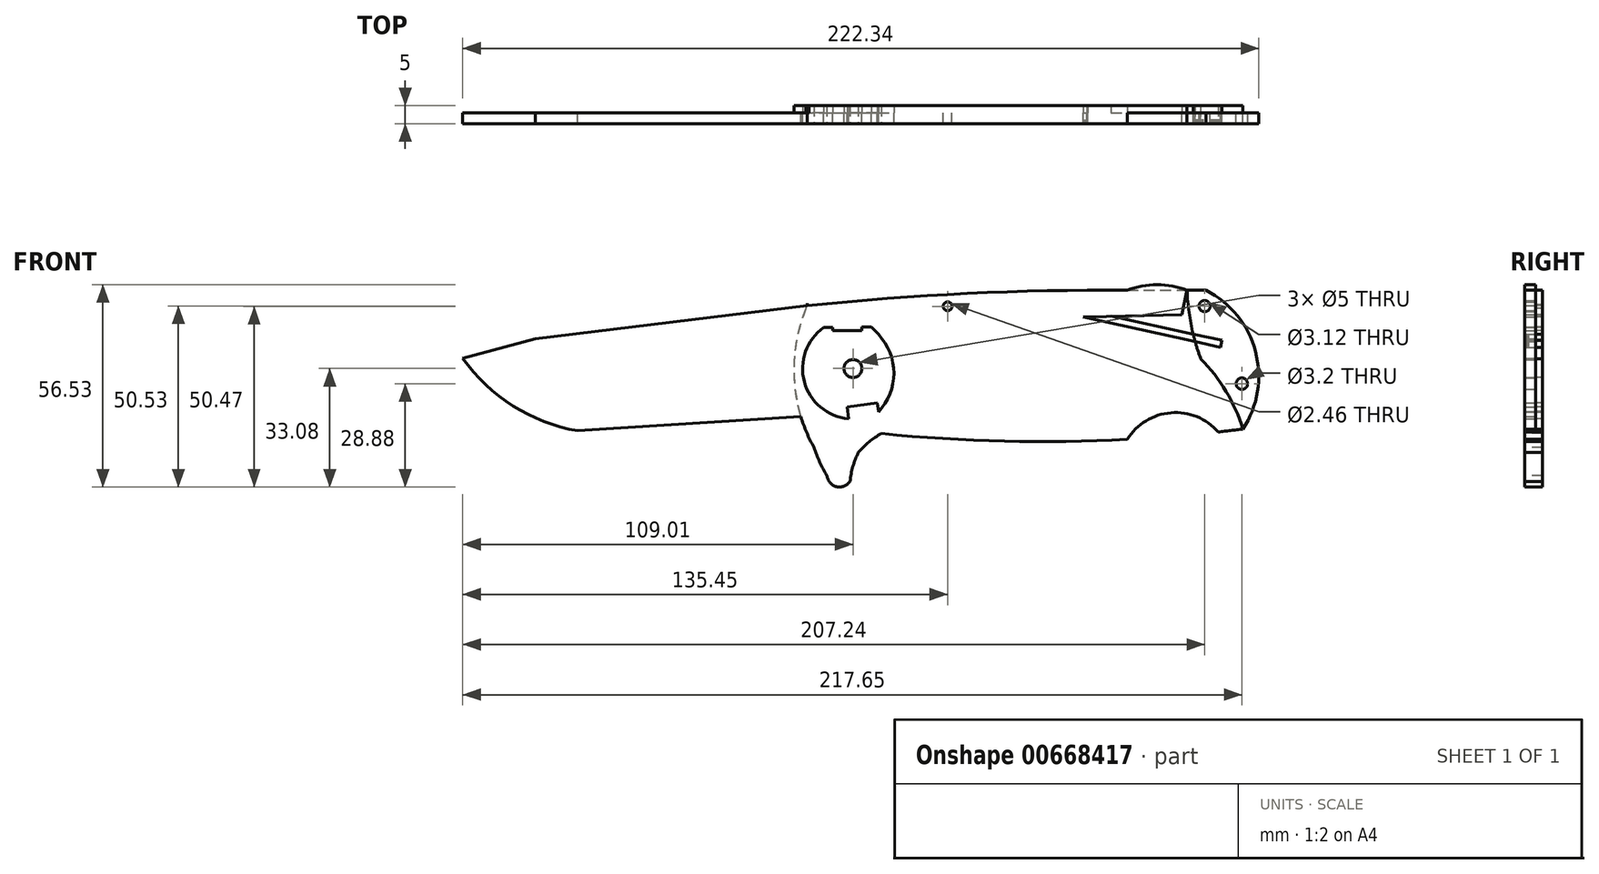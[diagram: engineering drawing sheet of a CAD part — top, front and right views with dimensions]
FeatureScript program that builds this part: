
annotation { "Feature Type Name" : "Feature", "Feature Type Description" : "" }
export const myFeature = defineFeature(function(context is Context, id is Id, definition is map)
    precondition{}
    {
        {
            var Q0;
            Q0=qCreatedBy(makeId("Front.planeOp"),FACE);
            var sketch = newSketch(context, id + "F0", { "sketchPlane" : qUnion([Q0])});
            skArc(sketch, "E0", {"start": v(38.96, -8.35) * mm, "mid": v(42.45, 13.33) * mm, "end": v(28.67, 30.42) * mm});
            skArc(sketch, "E1", {"start": v(-62.01, -9.6) * mm, "mid": v(-27.7, -11.74) * mm, "end": v(6.69, -11.23) * mm});
            skArc(sketch, "E2", {"start": v(-62.01, -9.6) * mm, "mid": v(-65.5, -11.93) * mm, "end": v(-68.47, -14.9) * mm});
            skArc(sketch, "E3", {"start": v(-80.85, -13.53) * mm, "mid": v(-79.28, -17.56) * mm, "end": v(-77.25, -21.38) * mm});
            skPoint(sketch, "E4.end.orphan", {"position": v(-73.1, -26.92) * mm});
            skArc(sketch, "E5", {"start": v(-77.25, -21.38) * mm, "mid": v(-74.57, -24.43) * mm, "end": v(-70.79, -22.98) * mm});
            skArc(sketch, "E6", {"start": v(-68.47, -14.9) * mm, "mid": v(-70, -18.84) * mm, "end": v(-70.79, -22.98) * mm});
            skCircle(sketch, "E7", {"center": v(-69.98, 8.55) * mm, "radius": 2.5 * mm});
            skArc(sketch, "E8", {"start": v(32.05, -9.17) * mm, "mid": v(18.85, -3.8) * mm, "end": v(6.69, -11.23) * mm});
            skArc(sketch, "E9.trimOffspring", {"start": v(32.05, -9.17) * mm, "mid": v(35.5, -8.77) * mm, "end": v(38.96, -8.35) * mm});
            skArc(sketch, "E10", {"start": v(6.66, 30.42) * mm, "mid": v(15, 26.76) * mm, "end": v(23.35, 30.42) * mm});
            skLineSegment(sketch, "E11.trimOffspring", {"start": v(23.35, 30.42) * mm, "end": v(28.67, 30.42) * mm});
            skArc(sketch, "E12", {"start": v(-82.74, 26.12) * mm, "mid": v(-86.44, 6.07) * mm, "end": v(-80.85, -13.53) * mm});
            skArc(sketch, "E13", {"start": v(6.66, 30.42) * mm, "mid": v(-38.1, 29.51) * mm, "end": v(-82.74, 26.12) * mm});
            skArc(sketch, "E14", {"start": v(23.35, 30.42) * mm, "mid": v(24.5, 20.7) * mm, "end": v(27.17, 11.28) * mm});
            skLineSegment(sketch, "E15", {"start": v(21.88, 23.6) * mm, "end": v(23.35, 30.42) * mm});
            skLineSegment(sketch, "E16", {"start": v(-74.78, 26.9) * mm, "end": v(-75.59, 21.45) * mm});
            skLineSegment(sketch, "E17", {"start": v(6.66, 30.42) * mm, "end": v(23.35, 30.42) * mm});
            skLineSegment(sketch, "E18.left", {"start": v(-75.59, 21.45) * mm, "end": v(-75.59, 19.1) * mm});
            skLineSegment(sketch, "E18.right", {"start": v(-67.57, 21.63) * mm, "end": v(-67.57, 19.2) * mm});
            skLineSegment(sketch, "E19", {"start": v(-67.57, 21.63) * mm, "end": v(21.88, 23.6) * mm});
            skCircle(sketch, "E20", {"center": v(-43.54, 25.94) * mm, "radius": 1.23 * mm});
            skLineSegment(sketch, "E21", {"start": v(25.06, 18.18) * mm, "end": v(2.12, 23.17) * mm});
            skLineSegment(sketch, "E22", {"start": v(2.12, 23.17) * mm, "end": v(33.07, 16.44) * mm});
            skLineSegment(sketch, "E23", {"start": v(33.07, 16.44) * mm, "end": v(32.65, 14.49) * mm});
            skLineSegment(sketch, "E24", {"start": v(32.65, 14.49) * mm, "end": v(-5.64, 23) * mm});
            skLineSegment(sketch, "E25", {"start": v(-5.64, 23) * mm, "end": v(-4.61, 23.02) * mm});
            skLineSegment(sketch, "E26", {"start": v(-4.61, 23.02) * mm, "end": v(2.8, 23.02) * mm});
            skArc(sketch, "E27", {"start": v(23.35, 30.42) * mm, "mid": v(15, 32) * mm, "end": v(6.66, 30.42) * mm});
            skLineSegment(sketch, "E28", {"start": v(-75.59, 21.45) * mm, "end": v(-75.59, 21.45) * mm});
            skPoint(sketch, "E29.end.orphan", {"position": v(-75.59, 20.8) * mm});
            skArc(sketch, "E30", {"start": v(-78.16, 19.99) * mm, "mid": v(-83.55, 4.86) * mm, "end": v(-71.25, -5.46) * mm});
            skLineSegment(sketch, "E31", {"start": v(-78.16, 19.99) * mm, "end": v(-75.59, 20.03) * mm});
            skPoint(sketch, "E32.end.orphan", {"position": v(-62.2, 20.27) * mm});
            skPoint(sketch, "E33.endSnap0", {"position": v(-66.22, 20.2) * mm});
            skPoint(sketch, "E34.orphan", {"position": v(-64.88, 20.22) * mm});
            skPoint(sketch, "E35.trimOffspring.start.orphan", {"position": v(-67.57, 20.17) * mm});
            skLineSegment(sketch, "E36", {"start": v(-67.57, 20.17) * mm, "end": v(-64.85, 20.19) * mm});
            skLineSegment(sketch, "E37", {"start": v(-67.57, 18.1) * mm, "end": v(-67.57, 17.95) * mm});
            skLineSegment(sketch, "E38", {"start": v(-75.59, 18.1) * mm, "end": v(-75.59, 17.95) * mm});
            skLineSegment(sketch, "E39", {"start": v(-75.59, 19.1) * mm, "end": v(-67.57, 19.2) * mm});
            skLineSegment(sketch, "E40", {"start": v(-64.88, 20.22) * mm, "end": v(-62.87, 18.1) * mm});
            skPoint(sketch, "E41.orphan", {"position": v(-62.87, 20.2) * mm});
            skLineSegment(sketch, "E42", {"start": v(-78.16, 19.99) * mm, "end": v(-82.74, 26.12) * mm});
            skLineSegment(sketch, "E43", {"start": v(-82.74, 26.12) * mm, "end": v(-82.74, 26.12) * mm});
            skPoint(sketch, "E44.start.orphan", {"position": v(-191.79, 19.58) * mm});
            skLineSegment(sketch, "E45", {"start": v(-84.04, -6.39) * mm, "end": v(-84, -6.38) * mm});
            skLineSegment(sketch, "E46", {"start": v(-75.59, 19.1) * mm, "end": v(-75.59, 17.95) * mm, "construction": true});
            skPoint(sketch, "E47.start.orphan", {"position": v(-84.04, -6.38) * mm});
            skArc(sketch, "E48", {"start": v(38.96, -8.35) * mm, "mid": v(34.25, 2.18) * mm, "end": v(27.17, 11.28) * mm});
            skPoint(sketch, "E49.orphan", {"position": v(-137.26, 22.85) * mm});
            skLineSegment(sketch, "E50", {"start": v(-74.9, 26.12) * mm, "end": v(-84.7, 25.19) * mm});
            skArc(sketch, "E51", {"start": v(-62.87, -3.59) * mm, "mid": v(-58.55, 7.25) * mm, "end": v(-62.87, 18.1) * mm});
            skLineSegment(sketch, "E52", {"start": v(-75.59, -4.35) * mm, "end": v(-146.9, -8.83) * mm});
            skArc(sketch, "E53", {"start": v(-178.99, 11.44) * mm, "mid": v(-164.95, -1.88) * mm, "end": v(-146.9, -8.83) * mm});
            skPoint(sketch, "E54.start.orphan", {"position": v(-176.27, 12.79) * mm});
            skCircle(sketch, "E55", {"center": v(38.66, 4.35) * mm, "radius": 1.6 * mm});
            skCircle(sketch, "E56", {"center": v(28.25, 26) * mm, "radius": 1.56 * mm});
            skPoint(sketch, "E57.endSnap0", {"position": v(-71.58, 19.15) * mm});
            skPoint(sketch, "E58.orphan", {"position": v(-70.1, 19.15) * mm});
            skLineSegment(sketch, "E59", {"start": v(-178.99, 11.44) * mm, "end": v(-158.64, 16.83) * mm});
            skPoint(sketch, "E60.orphan", {"position": v(-179.91, 12.79) * mm});
            skLineSegment(sketch, "E61", {"start": v(-82.74, 26.12) * mm, "end": v(-158.64, 16.83) * mm});
            skPoint(sketch, "E62.start.orphan", {"position": v(-75.59, -3.76) * mm});
            skLineSegment(sketch, "E63", {"start": v(-62.87, -3.48) * mm, "end": v(-62.87, -3.59) * mm});
            skLineSegment(sketch, "E64", {"start": v(-71.25, -5.46) * mm, "end": v(-71.6, -2.16) * mm});
            skLineSegment(sketch, "E65", {"start": v(-63.2, -1.04) * mm, "end": v(-71.6, -2.16) * mm});
            skLineSegment(sketch, "E66", {"start": v(-62.87, -3.48) * mm, "end": v(-63.2, -1.04) * mm});
            skSolve(sketch);
        }
        {
            var Q0;
            Q0=makeQuery(id+"F0.imprint","IMPRINT",FACE,{"disambiguationData":[TD([[makeQuery(id+"F0.imprint","IMPRINT",EDGE,{"derivedFrom":sQuery(id+"F0.wireOp",EDGE,"E0")}),1.0]])]});
            extrude(context, id + "F1", {"entities" : qUnion([Q0]), "depth" : 2.5 * mm, "offsetDistance" : 25 * mm});
        }
        {
            var Q0;
            Q0=makeQuery(id+"F1.opExtrude","SWEPT_EDGE",EDGE,{"disambiguationData":[OSD([sQuery(id+"F0.wireOp",EDGE,"E0"),sQuery(id+"F0.wireOp",EDGE,"E11.trimOffspring")])]});
            fillet(context, id + "F2", {"entities" : qUnion([Q0]), "radius" : 5 * mm, "tangentPropagation" : true, "allowEdgeOverflow" : false});
        }
        {
            var Q0;
            Q0=makeQuery(id+"F1.opExtrude","SWEPT_EDGE",EDGE,{"disambiguationData":[OSD([sQuery(id+"F0.wireOp",EDGE,"E0"),sQuery(id+"F0.wireOp",EDGE,"E9.trimOffspring")])]});
            fillet(context, id + "F3", {"entities" : qUnion([Q0]), "radius" : 5 * mm, "tangentPropagation" : true, "allowEdgeOverflow" : false});
        }
        {
            var Q0;
            Q0=makeQuery(id+"F0.imprint","IMPRINT",FACE,{"disambiguationData":[TD([[makeQuery(id+"F0.imprint","IMPRINT",EDGE,{"derivedFrom":sQuery(id+"F0.wireOp",EDGE,"E0")}),1.0]])]});
            extrude(context, id + "F4", {"entities" : qUnion([Q0]), "operationType" : NewBodyOperationType.ADD, "oppositeDirection" : true, "depth" : 3 * mm, "offsetDistance" : 25 * mm});
        }
        {
            var Q0;
            Q0=makeQuery(id+"F0.imprint","IMPRINT",FACE,{"disambiguationData":[TD([[makeQuery(id+"F0.imprint","IMPRINT",EDGE,{"derivedFrom":sQuery(id+"F0.wireOp",EDGE,"E10")}),1.0]])]});
            extrude(context, id + "F5", {"entities" : qUnion([Q0]), "depth" : 3 * mm, "offsetDistance" : 25 * mm});
        }
        {
            var Q0;
            {var subQ2=sQuery(id+"F0.wireOp",EDGE,"E10");Q0=makeQuery(id+"F0.imprint","IMPRINT",FACE,{"disambiguationData":[TD([[makeQuery(id+"F0.imprint","IMPRINT",EDGE,{"derivedFrom":subQ2}),-1.0]])]});}
            extrude(context, id + "F6", {"entities" : qUnion([Q0]), "depth" : 3 * mm, "offsetDistance" : 25 * mm});
        }
        {
            var Q0;
            {var subQ0=sQuery(id+"F0.wireOp",EDGE,"E25");Q0=makeQuery(id+"F0.imprint","IMPRINT",FACE,{"disambiguationData":[TD([[makeQuery(id+"F0.imprint","IMPRINT",EDGE,{"derivedFrom":subQ0}),-1.0]])]});}
            var Q1;
            {var subQ5=sQuery(id+"F0.wireOp",EDGE,"E23");Q1=makeQuery(id+"F0.imprint","IMPRINT",FACE,{"disambiguationData":[TD([[makeQuery(id+"F0.imprint","IMPRINT",EDGE,{"derivedFrom":subQ5}),-1.0]])]});}
            extrude(context, id + "F7", {"entities" : qUnion([Q0, Q1]), "depth" : 2 * mm, "offsetDistance" : 25 * mm});
        }
        {
            var Q0;
            Q0=makeQuery(id+"F0.imprint","IMPRINT",FACE,{"disambiguationData":[TD([[makeQuery(id+"F0.imprint","IMPRINT",EDGE,{"derivedFrom":sQuery(id+"F0.wireOp",EDGE,"E17")}),1.0]])]});
            extrude(context, id + "F8", {"entities" : qUnion([Q0]), "operationType" : NewBodyOperationType.ADD, "depth" : 3 * mm, "offsetDistance" : 25 * mm});
        }
        {
            var Q0;
            Q0=makeQuery(id+"F4.opExtrude","CAP_FACE",FACE,{"disambiguationData":[OSD([sQuery(id+"F0.wireOp",EDGE,"E0"),sQuery(id+"F0.wireOp",EDGE,"E11.trimOffspring"),sQuery(id+"F0.wireOp",EDGE,"E14"),sQuery(id+"F0.wireOp",EDGE,"E22"),sQuery(id+"F0.wireOp",EDGE,"E23"),sQuery(id+"F0.wireOp",EDGE,"E24")])],"isStart":false});
            extrude(context, id + "F9", {"entities" : qUnion([Q0]), "operationType" : NewBodyOperationType.ADD, "depth" : 1 * mm, "offsetDistance" : 25 * mm});
        }
        {
            var Q0;
            Q0=makeQuery(id+"F9.opExtrude","CAP_FACE",FACE,{"disambiguationData":[OSD([sQuery(id+"F0.wireOp",EDGE,"E0"),sQuery(id+"F0.wireOp",EDGE,"E11.trimOffspring"),sQuery(id+"F0.wireOp",EDGE,"E14"),sQuery(id+"F0.wireOp",EDGE,"E22"),sQuery(id+"F0.wireOp",EDGE,"E23"),sQuery(id+"F0.wireOp",EDGE,"E24")])],"isStart":false});
            extrude(context, id + "F10", {"entities" : qUnion([Q0]), "operationType" : NewBodyOperationType.REMOVE, "oppositeDirection" : true, "depth" : 2 * mm, "offsetDistance" : 25 * mm});
        }
        {
            var Q0;
            {var subQ11=sQuery(id+"F0.wireOp",EDGE,"E10");Q0=makeQuery(id+"F0.imprint","IMPRINT",FACE,{"disambiguationData":[TD([[makeQuery(id+"F0.imprint","IMPRINT",EDGE,{"derivedFrom":subQ11}),-1.0]])]});}
            var Q1;
            Q1=makeQuery(id+"F0.imprint","IMPRINT",FACE,{"disambiguationData":[TD([[makeQuery(id+"F0.imprint","IMPRINT",EDGE,{"derivedFrom":sQuery(id+"F0.wireOp",EDGE,"E10")}),1.0]])]});
            extrude(context, id + "F11", {"entities" : qUnion([Q0, Q1]), "oppositeDirection" : true, "depth" : 2.5 * mm, "offsetDistance" : 25 * mm});
        }
        {
            var Q0;
            Q0=makeQuery(id+"F0.imprint","IMPRINT",FACE,{"disambiguationData":[TD([[makeQuery(id+"F0.imprint","IMPRINT",EDGE,{"derivedFrom":sQuery(id+"F0.wireOp",EDGE,"d4K3JjEk-ksbC-rxim-k1ym-PkVV789aZZM4")}),-1.0]])]});
            var Q1;
            Q1=makeQuery(id+"F0.imprint","IMPRINT",FACE,{"disambiguationData":[TD([[makeQuery(id+"F0.imprint","IMPRINT",EDGE,{"derivedFrom":sQuery(id+"F0.wireOp",EDGE,"E7")}),-1.0]])]});
            var Q2;
            {var subQ1=sQuery(id+"F0.wireOp",EDGE,"E42");Q2=makeQuery(id+"F0.imprint","IMPRINT",FACE,{"disambiguationData":[TD([[makeQuery(id+"F0.imprint","IMPRINT",EDGE,{"derivedFrom":subQ1}),1.0]])]});}
            var Q3;
            {var subQ2=sQuery(id+"F0.wireOp",EDGE,"E16");Q3=makeQuery(id+"F0.imprint","IMPRINT",FACE,{"disambiguationData":[TD([[makeQuery(id+"F0.imprint","IMPRINT",EDGE,{"derivedFrom":subQ2}),-1.0]])]});}
            extrude(context, id + "F12", {"entities" : qUnion([Q0, Q1, Q2, Q3]), "depth" : 3 * mm, "offsetDistance" : 25 * mm});
        }
        {
            var Q0;
            {var subQ1=sQuery(id+"F0.wireOp",EDGE,"E31");Q0=makeQuery(id+"F0.imprint","IMPRINT",FACE,{"disambiguationData":[TD([[makeQuery(id+"F0.imprint","IMPRINT",EDGE,{"derivedFrom":subQ1}),1.0]])]});}
            var Q1;
            {var subQ3=sQuery(id+"F0.wireOp",EDGE,"E12");var subQ7=sQuery(id+"F0.wireOp",EDGE,"E50");var subQ9=makeQuery(id+"F0.imprint","INTERSECT",VERTEX,{"derivedFrom":[subQ3,subQ7]});Q1=makeQuery(id+"F0.imprint","IMPRINT",FACE,{"disambiguationData":[TD([[makeQuery(id+"F0.imprint","IMPRINT",EDGE,{"disambiguationData":[TD([[subQ9,-1.0]])],"derivedFrom":subQ3}),1.0]])]});}
            extrude(context, id + "F13", {"entities" : qUnion([Q0, Q1]), "oppositeDirection" : true, "depth" : 2.5 * mm, "offsetDistance" : 25 * mm});
        }
        {
            var Q0;
            Q0=makeQuery(id+"F11.opExtrude","SWEPT_BODY",BODY,{"disambiguationData":[OSD([sQuery(id+"F0.wireOp",EDGE,"E13"),sQuery(id+"F0.wireOp",EDGE,"E15"),sQuery(id+"F0.wireOp",EDGE,"E16"),sQuery(id+"F0.wireOp",EDGE,"E17"),sQuery(id+"F0.wireOp",EDGE,"E18.left"),sQuery(id+"F0.wireOp",EDGE,"E18.right"),sQuery(id+"F0.wireOp",EDGE,"E19"),sQuery(id+"F0.wireOp",EDGE,"E20"),sQuery(id+"F0.wireOp",EDGE,"E25"),sQuery(id+"F0.wireOp",EDGE,"E39")])]});
            var Q1;
            Q1=makeQuery(id+"F13.opExtrude","SWEPT_BODY",BODY,{"disambiguationData":[OSD([sQuery(id+"F0.wireOp",EDGE,"E12"),sQuery(id+"F0.wireOp",EDGE,"E16"),sQuery(id+"F0.wireOp",EDGE,"E18.left"),sQuery(id+"F0.wireOp",EDGE,"E30"),sQuery(id+"F0.wireOp",EDGE,"E31"),sQuery(id+"F0.wireOp",EDGE,"gyOXoMPe-yHgR-Amyv-KbJH-xM9F0bznGJoQ"),sQuery(id+"F0.wireOp",EDGE,"E50")])]});
            booleanBodies(context, id + "F14", {"operationType" : BooleanOperationType.UNION, "tools" : qUnion([Q0, Q1])});
        }
        {
            var Q0;
            Q0=makeQuery(id+"F0.imprint","IMPRINT",FACE,{"disambiguationData":[TD([[makeQuery(id+"F0.imprint","IMPRINT",EDGE,{"derivedFrom":sQuery(id+"F0.wireOp",EDGE,"E7")}),-1.0]])]});
            var Q1;
            {var subQ4=sQuery(id+"F0.wireOp",EDGE,"d76b19db-baf5-4d0a-8a79-8b2ea7cbffe1");Q1=makeQuery(id+"F0.imprint","IMPRINT",FACE,{"disambiguationData":[TD([[makeQuery(id+"F0.imprint","IMPRINT",EDGE,{"derivedFrom":subQ4}),-1.0]])]});}
            var Q2;
            {var subQ3=sQuery(id+"F0.wireOp",EDGE,"E12");var subQ7=sQuery(id+"F0.wireOp",EDGE,"E50");var subQ9=makeQuery(id+"F0.imprint","INTERSECT",VERTEX,{"derivedFrom":[subQ3,subQ7]});Q2=makeQuery(id+"F0.imprint","IMPRINT",FACE,{"disambiguationData":[TD([[makeQuery(id+"F0.imprint","IMPRINT",EDGE,{"disambiguationData":[TD([[subQ9,-1.0]])],"derivedFrom":subQ3}),1.0]])]});}
            extrude(context, id + "F15", {"entities" : qUnion([Q0, Q1, Q2]), "depth" : 3 * mm, "offsetDistance" : 25 * mm});
        }
        {
            var Q0;
            {var subQ1=sQuery(id+"F0.wireOp",EDGE,"E31");Q0=makeQuery(id+"F0.imprint","IMPRINT",FACE,{"disambiguationData":[TD([[makeQuery(id+"F0.imprint","IMPRINT",EDGE,{"derivedFrom":subQ1}),1.0]])]});}
            extrude(context, id + "F16", {"entities" : qUnion([Q0]), "depth" : 3 * mm, "offsetDistance" : 25 * mm});
        }
        {
            var Q0;
            Q0=makeQuery(id+"F0.imprint","IMPRINT",FACE,{"disambiguationData":[TD([[makeQuery(id+"F0.imprint","IMPRINT",EDGE,{"derivedFrom":sQuery(id+"F0.wireOp",EDGE,"E0")}),1.0]])]});
            extrude(context, id + "F17", {"entities" : qUnion([Q0]), "depth" : 25 * mm, "offsetDistance" : 25 * mm});
        }
        {
            var Q0;
            {var subQ4=sQuery(id+"F0.wireOp",EDGE,"d76b19db-baf5-4d0a-8a79-8b2ea7cbffe1");Q0=makeQuery(id+"F0.imprint","IMPRINT",FACE,{"disambiguationData":[TD([[makeQuery(id+"F0.imprint","IMPRINT",EDGE,{"derivedFrom":subQ4}),-1.0]])]});}
            var Q1;
            Q1=makeQuery(id+"F0.imprint","IMPRINT",FACE,{"disambiguationData":[TD([[makeQuery(id+"F0.imprint","IMPRINT",EDGE,{"derivedFrom":sQuery(id+"F0.wireOp",EDGE,"E7")}),-1.0]])]});
            var Q2;
            Q2=makeQuery(id+"F0.imprint","IMPRINT",FACE,{"disambiguationData":[TD([[makeQuery(id+"F0.imprint","IMPRINT",EDGE,{"derivedFrom":sQuery(id+"F0.wireOp",EDGE,"E33")}),-1.0]])]});
            var Q3;
            {var subQ1=sQuery(id+"F0.wireOp",EDGE,"E31");Q3=makeQuery(id+"F0.imprint","IMPRINT",FACE,{"disambiguationData":[TD([[makeQuery(id+"F0.imprint","IMPRINT",EDGE,{"derivedFrom":subQ1}),1.0]])]});}
            var Q4;
            {var subQ3=sQuery(id+"F0.wireOp",EDGE,"E12");var subQ7=sQuery(id+"F0.wireOp",EDGE,"E50");var subQ9=makeQuery(id+"F0.imprint","INTERSECT",VERTEX,{"derivedFrom":[subQ3,subQ7]});Q4=makeQuery(id+"F0.imprint","IMPRINT",FACE,{"disambiguationData":[TD([[makeQuery(id+"F0.imprint","IMPRINT",EDGE,{"disambiguationData":[TD([[subQ9,-1.0]])],"derivedFrom":subQ3}),1.0]])]});}
            extrude(context, id + "F18", {"entities" : qUnion([Q0, Q1, Q2, Q3, Q4]), "depth" : 3 * mm, "offsetDistance" : 25 * mm});
        }
        {
            var Q0;
            Q0=makeQuery(id+"F17.opExtrude","CAP_FACE",FACE,{"disambiguationData":[OSD([sQuery(id+"F0.wireOp",EDGE,"E0"),sQuery(id+"F0.wireOp",EDGE,"E11.trimOffspring"),sQuery(id+"F0.wireOp",EDGE,"E14"),sQuery(id+"F0.wireOp",EDGE,"E22"),sQuery(id+"F0.wireOp",EDGE,"E23"),sQuery(id+"F0.wireOp",EDGE,"E24"),sQuery(id+"F0.wireOp",EDGE,"E48")])],"isStart":false});
            extrude(context, id + "F19", {"entities" : qUnion([Q0]), "operationType" : NewBodyOperationType.REMOVE, "oppositeDirection" : true, "depth" : 2 * mm, "offsetDistance" : 25 * mm});
        }
        {
            var Q0;
            Q0=makeQuery(id+"F19.boolean.opBoolean","COPY",FACE,{"derivedFrom":makeQuery(id+"F19.opExtrude","CAP_FACE",FACE,{"disambiguationData":[OSD([sQuery(id+"F0.wireOp",EDGE,"E0"),sQuery(id+"F0.wireOp",EDGE,"E11.trimOffspring"),sQuery(id+"F0.wireOp",EDGE,"E14"),sQuery(id+"F0.wireOp",EDGE,"E22"),sQuery(id+"F0.wireOp",EDGE,"E23"),sQuery(id+"F0.wireOp",EDGE,"E24"),sQuery(id+"F0.wireOp",EDGE,"E48")])],"isStart":false})});
            extrude(context, id + "F20", {"entities" : qUnion([Q0]), "operationType" : NewBodyOperationType.REMOVE, "oppositeDirection" : true, "depth" : 25 * mm, "offsetDistance" : 25 * mm});
        }
        {
            var Q0;
            Q0=makeQuery(id+"F0.imprint","IMPRINT",FACE,{"disambiguationData":[TD([[makeQuery(id+"F0.imprint","IMPRINT",EDGE,{"derivedFrom":sQuery(id+"F0.wireOp",EDGE,"E0")}),1.0]])]});
            extrude(context, id + "F21", {"entities" : qUnion([Q0]), "depth" : 3 * mm, "offsetDistance" : 25 * mm});
        }
        {
            var Q0;
            Q0=makeQuery(id+"F13.opExtrude","SWEPT_FACE",FACE,{"disambiguationData":[OSD([sQuery(id+"F0.wireOp",EDGE,"E50")])]});
            extrude(context, id + "F22", {"entities" : qUnion([Q0]), "operationType" : NewBodyOperationType.ADD, "depth" : 1 * mm, "offsetDistance" : 25 * mm});
        }
        {
            var Q0;
            Q0=makeQuery(id+"F22.opExtrude","CAP_FACE",FACE,{"disambiguationData":[OSD([sQuery(id+"F0.wireOp",EDGE,"E50")])],"isStart":false});
            extrude(context, id + "F23", {"entities" : qUnion([Q0]), "operationType" : NewBodyOperationType.ADD, "oppositeDirection" : true, "depth" : 1 * mm, "offsetDistance" : 25 * mm});
        }
        {
            var Q0;
            {var subQ0=sQuery(id+"F0.wireOp",EDGE,"E50");var subQ1=sQuery(id+"F0.wireOp",EDGE,"E18.left");var subQ2=sQuery(id+"F0.wireOp",EDGE,"E16");Q0=makeQuery(id+"F22.boolean.opBoolean","MERGE",FACE,{"derivedFrom":[makeQuery(id+"F14.opBoolean","MERGE",FACE,{"derivedFrom":[makeQuery(id+"F11.opExtrude","CAP_FACE",FACE,{"disambiguationData":[OSD([sQuery(id+"F0.wireOp",EDGE,"E13"),sQuery(id+"F0.wireOp",EDGE,"E15"),subQ2,sQuery(id+"F0.wireOp",EDGE,"E17"),subQ1,sQuery(id+"F0.wireOp",EDGE,"E18.right"),sQuery(id+"F0.wireOp",EDGE,"E19"),sQuery(id+"F0.wireOp",EDGE,"E20"),sQuery(id+"F0.wireOp",EDGE,"E25"),sQuery(id+"F0.wireOp",EDGE,"E39")])],"isStart":false}),makeQuery(id+"F13.opExtrude","CAP_FACE",FACE,{"disambiguationData":[OSD([sQuery(id+"F0.wireOp",EDGE,"E12"),subQ2,subQ1,sQuery(id+"F0.wireOp",EDGE,"E30"),sQuery(id+"F0.wireOp",EDGE,"E31"),sQuery(id+"F0.wireOp",EDGE,"gyOXoMPe-yHgR-Amyv-KbJH-xM9F0bznGJoQ"),subQ0])],"isStart":false})]}),makeQuery(id+"F22.opExtrude","SWEPT_FACE",FACE,{"disambiguationData":[OSD([subQ0]),TDD([makeQuery(id+"F13.opExtrude","CAP_EDGE",EDGE,{"disambiguationData":[OSD([subQ0])],"isStart":false})])]})]});}
            extrude(context, id + "F24", {"entities" : qUnion([Q0]), "operationType" : NewBodyOperationType.REMOVE, "oppositeDirection" : true, "depth" : 0.5 * mm, "offsetDistance" : 25 * mm});
        }
        {
            var Q0;
            {var subQ5=sQuery(id+"F0.wireOp",EDGE,"E23");Q0=makeQuery(id+"F0.imprint","IMPRINT",FACE,{"disambiguationData":[TD([[makeQuery(id+"F0.imprint","IMPRINT",EDGE,{"derivedFrom":subQ5}),-1.0]])]});}
            var Q1;
            {var subQ0=sQuery(id+"F0.wireOp",EDGE,"E25");Q1=makeQuery(id+"F0.imprint","IMPRINT",FACE,{"disambiguationData":[TD([[makeQuery(id+"F0.imprint","IMPRINT",EDGE,{"derivedFrom":subQ0}),-1.0]])]});}
            extrude(context, id + "F25", {"entities" : qUnion([Q0, Q1]), "depth" : 2.5 * mm, "offsetDistance" : 25 * mm});
        }
        {
            var Q0;
            {var subQ5=sQuery(id+"F0.wireOp",EDGE,"E23");Q0=makeQuery(id+"F0.imprint","IMPRINT",FACE,{"disambiguationData":[TD([[makeQuery(id+"F0.imprint","IMPRINT",EDGE,{"derivedFrom":subQ5}),-1.0]])]});}
            var Q1;
            {var subQ0=sQuery(id+"F0.wireOp",EDGE,"E25");Q1=makeQuery(id+"F0.imprint","IMPRINT",FACE,{"disambiguationData":[TD([[makeQuery(id+"F0.imprint","IMPRINT",EDGE,{"derivedFrom":subQ0}),-1.0]])]});}
            extrude(context, id + "F26", {"entities" : qUnion([Q0, Q1]), "oppositeDirection" : true, "depth" : 2 * mm, "offsetDistance" : 25 * mm});
        }
        {
            var Q0;
            Q0=makeQuery(id+"F0.imprint","IMPRINT",FACE,{"disambiguationData":[TD([[makeQuery(id+"F0.imprint","IMPRINT",EDGE,{"derivedFrom":sQuery(id+"F0.wireOp",EDGE,"E1")}),1.0]])]});
            extrude(context, id + "F27", {"entities" : qUnion([Q0]), "oppositeDirection" : true, "depth" : 2 * mm, "offsetDistance" : 25 * mm});
        }
        {
            var Q0;
            Q0=makeQuery(id+"F0.imprint","IMPRINT",FACE,{"disambiguationData":[TD([[makeQuery(id+"F0.imprint","IMPRINT",EDGE,{"derivedFrom":sQuery(id+"F0.wireOp",EDGE,"E7")}),-1.0]])]});
            extrude(context, id + "F28", {"entities" : qUnion([Q0]), "oppositeDirection" : true, "depth" : 2 * mm, "offsetDistance" : 25 * mm});
        }
        {
            var Q0;
            {var subQ1=sQuery(id+"F0.wireOp",EDGE,"E15");Q0=makeQuery(id+"F0.imprint","IMPRINT",FACE,{"disambiguationData":[TD([[makeQuery(id+"F0.imprint","IMPRINT",EDGE,{"derivedFrom":subQ1}),-1.0]])]});}
            extrude(context, id + "F29", {"entities" : qUnion([Q0]), "oppositeDirection" : true, "depth" : 2 * mm, "offsetDistance" : 25 * mm});
        }
        {
            var Q0;
            {var subQ0=sQuery(id+"F0.wireOp",EDGE,"E53");Q0=makeQuery(id+"F0.imprint","IMPRINT",FACE,{"disambiguationData":[TD([[makeQuery(id+"F0.imprint","IMPRINT",EDGE,{"derivedFrom":subQ0}),1.0]])]});}
            extrude(context, id + "F30", {"entities" : qUnion([Q0]), "operationType" : NewBodyOperationType.ADD, "depth" : 3 * mm, "offsetDistance" : 25 * mm});
        }
    });
